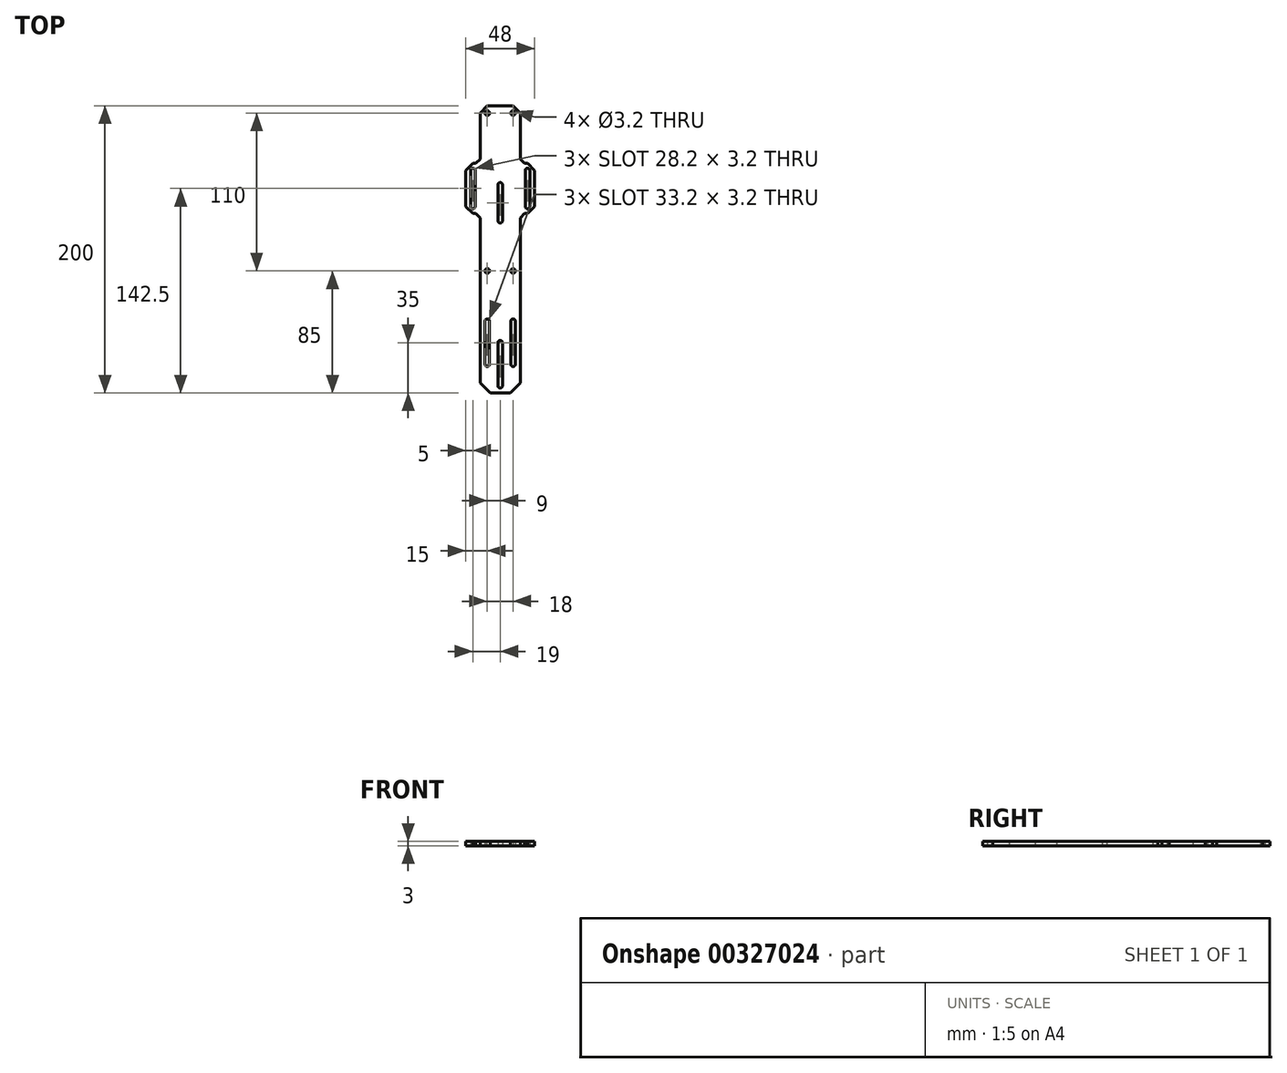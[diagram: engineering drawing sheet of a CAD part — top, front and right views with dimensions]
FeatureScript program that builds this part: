
annotation { "Feature Type Name" : "Feature", "Feature Type Description" : "" }
export const myFeature = defineFeature(function(context is Context, id is Id, definition is map)
    precondition{}
    {
        {
            var Q0;
            Q0=qCreatedBy(makeId("Top.planeOp"),FACE);
            var sketch = newSketch(context, id + "F0", { "sketchPlane" : qUnion([Q0])});
            skLineSegment(sketch, "E0.bottom", {"start": v(14, 100) * mm, "end": v(-14, 100) * mm});
            skLineSegment(sketch, "E0.top", {"start": v(14, -100) * mm, "end": v(-14, -100) * mm});
            skLineSegment(sketch, "E0.left", {"start": v(14, 100) * mm, "end": v(14, -100) * mm});
            skLineSegment(sketch, "E0.right", {"start": v(-14, 100) * mm, "end": v(-14, -100) * mm});
            skPoint(sketch, "E0.middle", {"position": v(0, 0) * mm});
            skCircle(sketch, "E1", {"center": v(9, 95) * mm, "radius": 1.6 * mm});
            skLineSegment(sketch, "E2.bottom", {"start": v(24, 25) * mm, "end": v(-24, 25) * mm});
            skLineSegment(sketch, "E2.top", {"start": v(24, 60) * mm, "end": v(-24, 60) * mm});
            skLineSegment(sketch, "E2.left", {"start": v(24, 25) * mm, "end": v(24, 60) * mm});
            skLineSegment(sketch, "E2.right", {"start": v(-24, 25) * mm, "end": v(-24, 60) * mm});
            skPoint(sketch, "E2.middle", {"position": v(0, 42.5) * mm});
            skCircle(sketch, "E3", {"center": v(0, 20) * mm, "radius": 1.6 * mm});
            skCircle(sketch, "E4", {"center": v(0, 45) * mm, "radius": 1.6 * mm});
            skCircle(sketch, "E5", {"center": v(19, 55) * mm, "radius": 1.6 * mm});
            skCircle(sketch, "E6", {"center": v(19, 30) * mm, "radius": 1.6 * mm});
            skLineSegment(sketch, "E7", {"start": v(1.6, 45) * mm, "end": v(1.6, 20) * mm});
            skLineSegment(sketch, "E8", {"start": v(17.4, 55) * mm, "end": v(17.4, 30) * mm});
            skLineSegment(sketch, "E9", {"start": v(20.6, 30) * mm, "end": v(20.6, 55) * mm});
            skCircle(sketch, "E10", {"center": v(0, -95) * mm, "radius": 1.6 * mm});
            skCircle(sketch, "E11", {"center": v(9, -80) * mm, "radius": 1.6 * mm});
            skCircle(sketch, "E12", {"center": v(9, -50) * mm, "radius": 1.6 * mm});
            skCircle(sketch, "E13", {"center": v(0, -65) * mm, "radius": 1.6 * mm});
            skLineSegment(sketch, "E14", {"start": v(1.6, -65) * mm, "end": v(1.6, -95) * mm});
            skLineSegment(sketch, "E15", {"start": v(7.4, -50) * mm, "end": v(7.4, -80) * mm});
            skLineSegment(sketch, "E16", {"start": v(10.6, -50) * mm, "end": v(10.6, -80) * mm});
            skCircle(sketch, "E17", {"center": v(9, -15) * mm, "radius": 1.6 * mm});
            skCircle(sketch, "E18.MirrorC", {"center": v(-9, 95) * mm, "radius": 1.6 * mm});
            skLineSegment(sketch, "E19.MirrorCS", {"start": v(-1.6, 45) * mm, "end": v(-1.6, 20) * mm});
            skCircle(sketch, "E20.MirrorC", {"center": v(-19, 55) * mm, "radius": 1.6 * mm});
            skLineSegment(sketch, "E21.MirrorCS", {"start": v(-17.4, 55) * mm, "end": v(-17.4, 30) * mm});
            skLineSegment(sketch, "E22.MirrorCS", {"start": v(-20.6, 30) * mm, "end": v(-20.6, 55) * mm});
            skCircle(sketch, "E23.MirrorC", {"center": v(-19, 30) * mm, "radius": 1.6 * mm});
            skCircle(sketch, "E24.MirrorC", {"center": v(-9, -15) * mm, "radius": 1.6 * mm});
            skCircle(sketch, "E25.MirrorC", {"center": v(-9, -50) * mm, "radius": 1.6 * mm});
            skLineSegment(sketch, "E26.MirrorCS", {"start": v(-10.6, -50) * mm, "end": v(-10.6, -80) * mm});
            skLineSegment(sketch, "E27.MirrorCS", {"start": v(-7.4, -50) * mm, "end": v(-7.4, -80) * mm});
            skCircle(sketch, "E28.MirrorC", {"center": v(-9, -80) * mm, "radius": 1.6 * mm});
            skLineSegment(sketch, "E29.MirrorCS", {"start": v(-1.6, -65) * mm, "end": v(-1.6, -95) * mm});
            skSolve(sketch);
        }
        {
            var Q0;
            Q0 = qSketchRegion(id + "F0", true);
            var Q1;
            {var subQ18=sQuery(id+"F0.wireOp",EDGE,"E0.top");Q1=makeQuery(id+"F0.imprint","IMPRINT",FACE,{"disambiguationData":[TD([[makeQuery(id+"F0.imprint","IMPRINT",EDGE,{"derivedFrom":subQ18}),-1.0]])]});}
            extrude(context, id + "F1", {"entities" : qUnion([Q0, Q1]), "depth" : 3 * mm});
        }
        {
            var Q0;
            Q0=makeQuery(id+"F1.opExtrude","SWEPT_EDGE",EDGE,{"disambiguationData":[OSD([sQuery(id+"F0.wireOp",EDGE,"E0.bottom"),sQuery(id+"F0.wireOp",EDGE,"E0.right")])]});
            var Q1;
            Q1=makeQuery(id+"F1.opExtrude","SWEPT_EDGE",EDGE,{"disambiguationData":[OSD([sQuery(id+"F0.wireOp",EDGE,"E0.bottom"),sQuery(id+"F0.wireOp",EDGE,"E0.left")])]});
            var Q2;
            Q2=makeQuery(id+"F1.opExtrude","SWEPT_EDGE",EDGE,{"disambiguationData":[OSD([sQuery(id+"F0.wireOp",EDGE,"E2.top"),sQuery(id+"F0.wireOp",EDGE,"E2.right")])]});
            var Q3;
            Q3=makeQuery(id+"F1.opExtrude","SWEPT_EDGE",EDGE,{"disambiguationData":[OSD([sQuery(id+"F0.wireOp",EDGE,"E2.top"),sQuery(id+"F0.wireOp",EDGE,"E2.left")])]});
            var Q4;
            Q4=makeQuery(id+"F1.opExtrude","SWEPT_EDGE",EDGE,{"disambiguationData":[OSD([sQuery(id+"F0.wireOp",EDGE,"E2.bottom"),sQuery(id+"F0.wireOp",EDGE,"E2.right")])]});
            var Q5;
            Q5=makeQuery(id+"F1.opExtrude","SWEPT_EDGE",EDGE,{"disambiguationData":[OSD([sQuery(id+"F0.wireOp",EDGE,"E2.bottom"),sQuery(id+"F0.wireOp",EDGE,"E2.left")])]});
            chamfer(context, id + "F2", {"entities" : qUnion([Q0, Q1, Q2, Q3, Q4, Q5]), "width" : 5 * mm, "tangentPropagation" : true});
        }
        {
            var Q0;
            Q0=makeQuery(id+"F1.opExtrude","SWEPT_EDGE",EDGE,{"disambiguationData":[OSD([sQuery(id+"F0.wireOp",EDGE,"E0.left"),sQuery(id+"F0.wireOp",EDGE,"E2.bottom")])]});
            var Q1;
            Q1=makeQuery(id+"F1.opExtrude","SWEPT_EDGE",EDGE,{"disambiguationData":[OSD([sQuery(id+"F0.wireOp",EDGE,"E0.right"),sQuery(id+"F0.wireOp",EDGE,"E2.bottom")])]});
            var Q2;
            Q2=makeQuery(id+"F1.opExtrude","SWEPT_EDGE",EDGE,{"disambiguationData":[OSD([sQuery(id+"F0.wireOp",EDGE,"E0.right"),sQuery(id+"F0.wireOp",EDGE,"E2.top")])]});
            var Q3;
            Q3=makeQuery(id+"F1.opExtrude","SWEPT_EDGE",EDGE,{"disambiguationData":[OSD([sQuery(id+"F0.wireOp",EDGE,"E0.left"),sQuery(id+"F0.wireOp",EDGE,"E2.top")])]});
            chamfer(context, id + "F3", {"entities" : qUnion([Q0, Q1, Q2, Q3]), "width" : 3 * mm, "tangentPropagation" : true});
        }
        {
            var Q0;
            Q0=makeQuery(id+"F1.opExtrude","SWEPT_EDGE",EDGE,{"disambiguationData":[OSD([sQuery(id+"F0.wireOp",EDGE,"E0.top"),sQuery(id+"F0.wireOp",EDGE,"E0.left")])]});
            var Q1;
            Q1=makeQuery(id+"F1.opExtrude","SWEPT_EDGE",EDGE,{"disambiguationData":[OSD([sQuery(id+"F0.wireOp",EDGE,"E0.top"),sQuery(id+"F0.wireOp",EDGE,"E0.right")])]});
            chamfer(context, id + "F4", {"entities" : qUnion([Q0, Q1]), "width" : 7 * mm, "tangentPropagation" : true});
        }
    });
